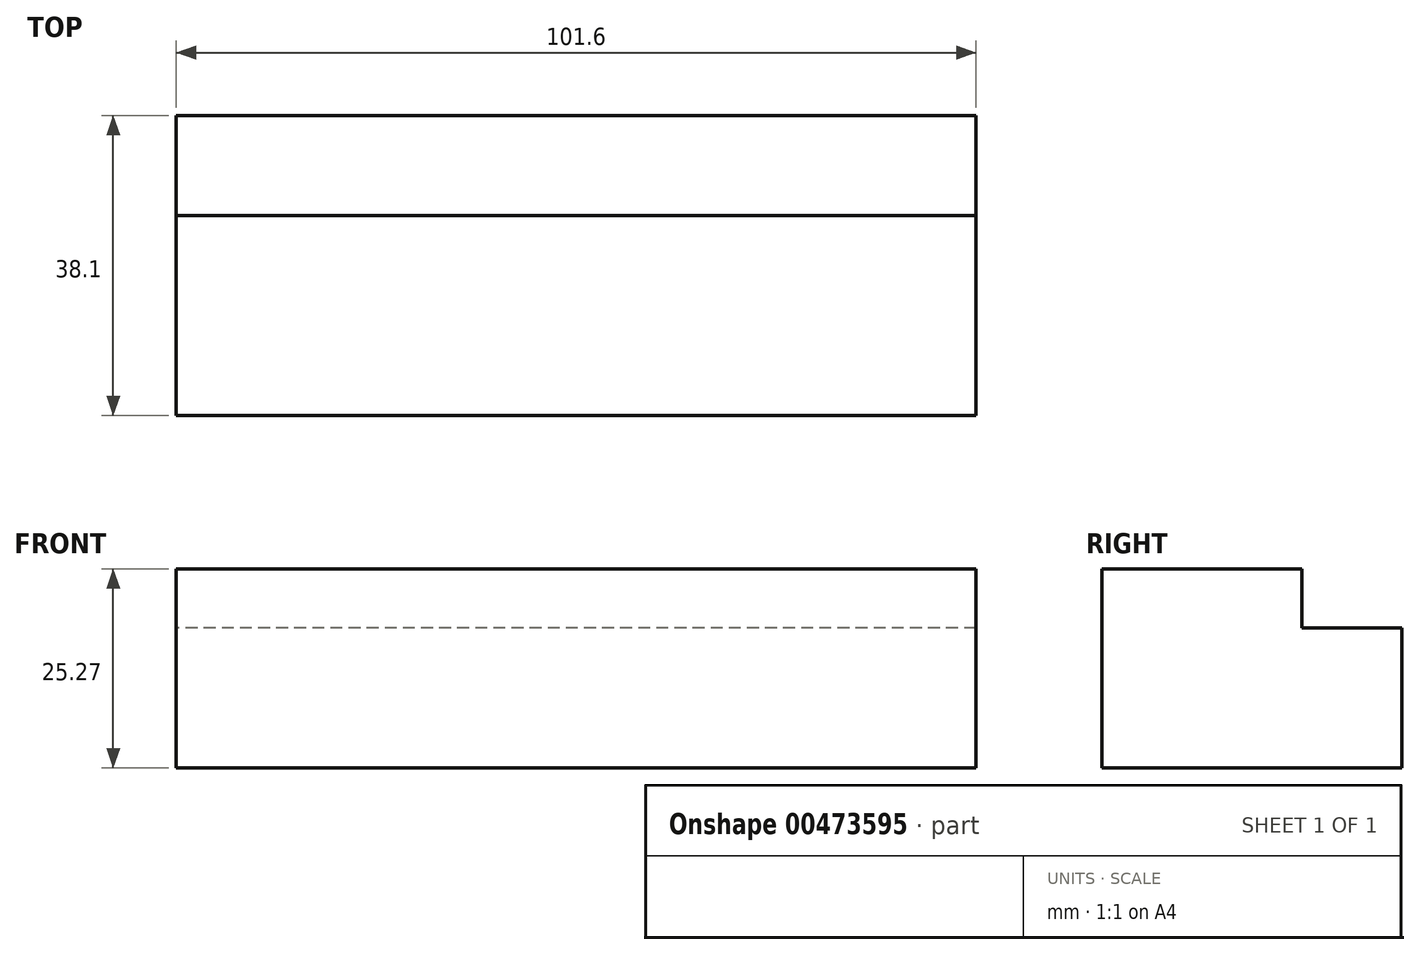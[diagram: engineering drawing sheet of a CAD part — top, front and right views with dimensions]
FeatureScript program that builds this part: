
annotation { "Feature Type Name" : "Feature", "Feature Type Description" : "" }
export const myFeature = defineFeature(function(context is Context, id is Id, definition is map)
    precondition{}
    {
        {
            var Q0;
            Q0=qCreatedBy(makeId("Right.planeOp"),FACE);
            var sketch = newSketch(context, id + "F0", { "sketchPlane" : qUnion([Q0])});
            skLineSegment(sketch, "E0", {"start": v(-38.1, 0) * mm, "end": v(0, 0) * mm});
            skLineSegment(sketch, "E1", {"start": v(-38.1, 0) * mm, "end": v(-38.1, 25.27) * mm});
            skLineSegment(sketch, "E2", {"start": v(-38.1, 25.27) * mm, "end": v(-12.7, 25.27) * mm});
            skLineSegment(sketch, "E3", {"start": v(-12.7, 25.27) * mm, "end": v(-12.7, 17.78) * mm});
            skLineSegment(sketch, "E4", {"start": v(-12.7, 17.78) * mm, "end": v(0, 17.78) * mm});
            skLineSegment(sketch, "E5", {"start": v(0, 17.78) * mm, "end": v(0, 0) * mm});
            skSolve(sketch);
        }
        {
            var Q0;
            Q0 = qSketchRegion(id + "F0", true);
            extrude(context, id + "F1", {"entities" : qUnion([Q0]), "depth" : 101.6 * mm});
        }
    });
